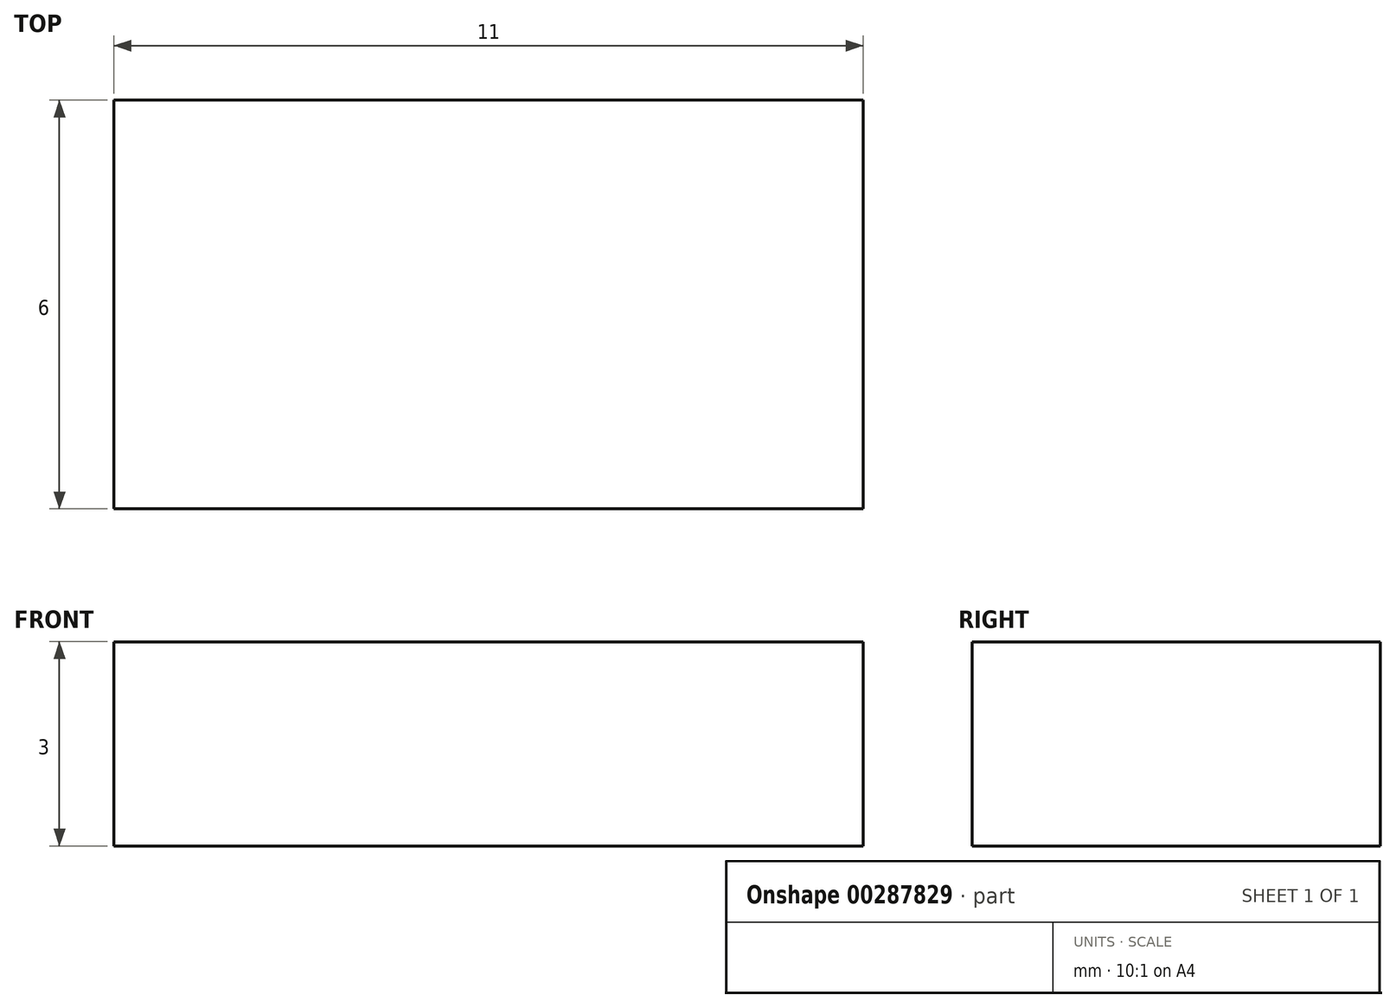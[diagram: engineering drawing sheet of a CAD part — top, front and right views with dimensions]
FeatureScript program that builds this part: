
annotation { "Feature Type Name" : "Feature", "Feature Type Description" : "" }
export const myFeature = defineFeature(function(context is Context, id is Id, definition is map)
    precondition{}
    {
        {
            var Q0;
            Q0=qCreatedBy(makeId("Front.planeOp"),FACE);
            var sketch = newSketch(context, id + "F0", { "sketchPlane" : qUnion([Q0])});
            skLineSegment(sketch, "E0.bottom", {"start": v(-54, 26.7) * mm, "end": v(-65, 26.7) * mm});
            skLineSegment(sketch, "E0.top", {"start": v(-54, 29.7) * mm, "end": v(-65, 29.7) * mm});
            skLineSegment(sketch, "E0.left", {"start": v(-54, 26.7) * mm, "end": v(-54, 29.7) * mm});
            skLineSegment(sketch, "E0.right", {"start": v(-65, 26.7) * mm, "end": v(-65, 29.7) * mm});
            skPoint(sketch, "E0.middle", {"position": v(-59.5, 28.2) * mm});
            skSolve(sketch);
        }
        {
            var Q0;
            Q0 = qSketchRegion(id + "F0", true);
            extrude(context, id + "F1", {"entities" : qUnion([Q0]), "depth" : 6 * mm});
        }
    });
